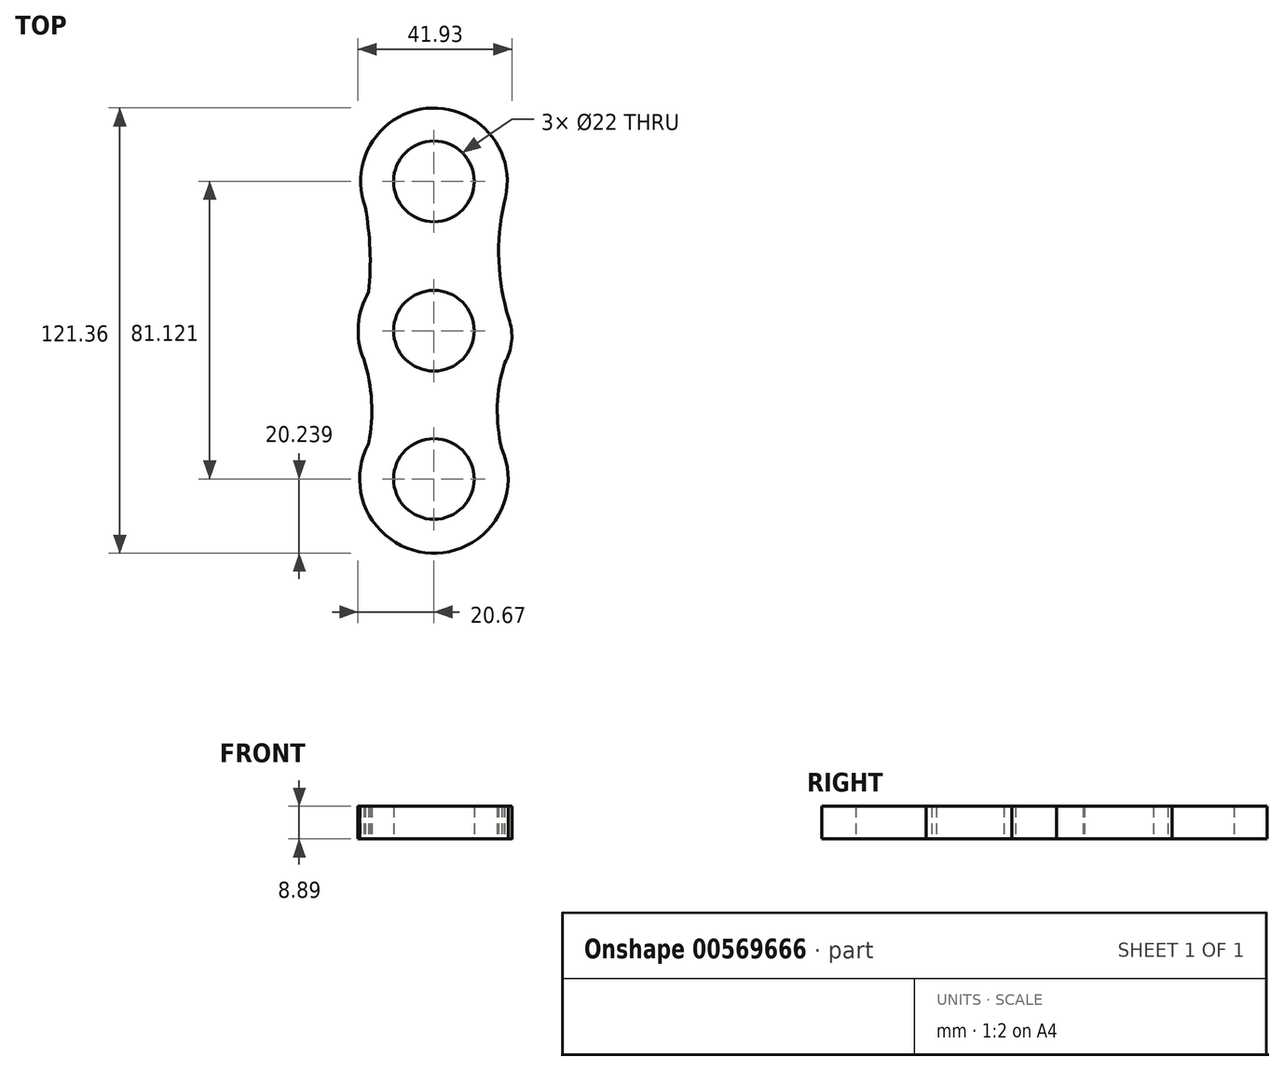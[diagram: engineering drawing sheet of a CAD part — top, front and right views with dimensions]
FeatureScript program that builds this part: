
annotation { "Feature Type Name" : "Feature", "Feature Type Description" : "" }
export const myFeature = defineFeature(function(context is Context, id is Id, definition is map)
    precondition{}
    {
        {
            var Q0;
            Q0=qCreatedBy(makeId("Top.planeOp"),FACE);
            var sketch = newSketch(context, id + "F0", { "sketchPlane" : qUnion([Q0])});
            skCircle(sketch, "E0", {"center": v(0, 40.72) * mm, "radius": 11 * mm});
            skCircle(sketch, "E1", {"center": v(0, 0) * mm, "radius": 11 * mm});
            skCircle(sketch, "E2", {"center": v(0, -40.4) * mm, "radius": 11 * mm});
            skArc(sketch, "E3", {"start": v(19.1, 34.8) * mm, "mid": v(-0.57, 60.7) * mm, "end": v(-18.73, 33.7) * mm});
            skArc(sketch, "E4", {"start": v(-17.76, 10.58) * mm, "mid": v(-20.61, 1.54) * mm, "end": v(-19.13, -7.83) * mm});
            skArc(sketch, "E5", {"start": v(-17.8, -30.76) * mm, "mid": v(-0.82, -60.62) * mm, "end": v(18.52, -32.24) * mm});
            skArc(sketch, "E6", {"start": v(-17.8, -30.76) * mm, "mid": v(-17, -19.21) * mm, "end": v(-19.13, -7.83) * mm});
            skArc(sketch, "E7", {"start": v(-17.76, 10.58) * mm, "mid": v(-17.44, 22.18) * mm, "end": v(-18.73, 33.7) * mm});
            skArc(sketch, "E8", {"start": v(19.1, 34.8) * mm, "mid": v(17.7, 19) * mm, "end": v(20.4, 3.37) * mm});
            skArc(sketch, "E9", {"start": v(19.26, -8.87) * mm, "mid": v(17.3, -20.5) * mm, "end": v(18.52, -32.24) * mm});
            skArc(sketch, "E10.trimOffspring", {"start": v(20.4, 3.37) * mm, "mid": v(19.94, 5.42) * mm, "end": v(19.29, 7.43) * mm});
            skArc(sketch, "E11", {"start": v(19.26, -8.87) * mm, "mid": v(21.2, -2.88) * mm, "end": v(20.4, 3.37) * mm});
            skSolve(sketch);
        }
        {
            var Q0;
            Q0=makeQuery(id+"F0.imprint","IMPRINT",FACE,{"disambiguationData":[TD([[makeQuery(id+"F0.imprint","IMPRINT",EDGE,{"derivedFrom":sQuery(id+"F0.wireOp",EDGE,"E0")}),-1.0]])]});
            extrude(context, id + "F1", {"entities" : qUnion([Q0]), "depth" : 8.9 * mm, "offsetDistance" : 25.4 * mm});
        }
    });
